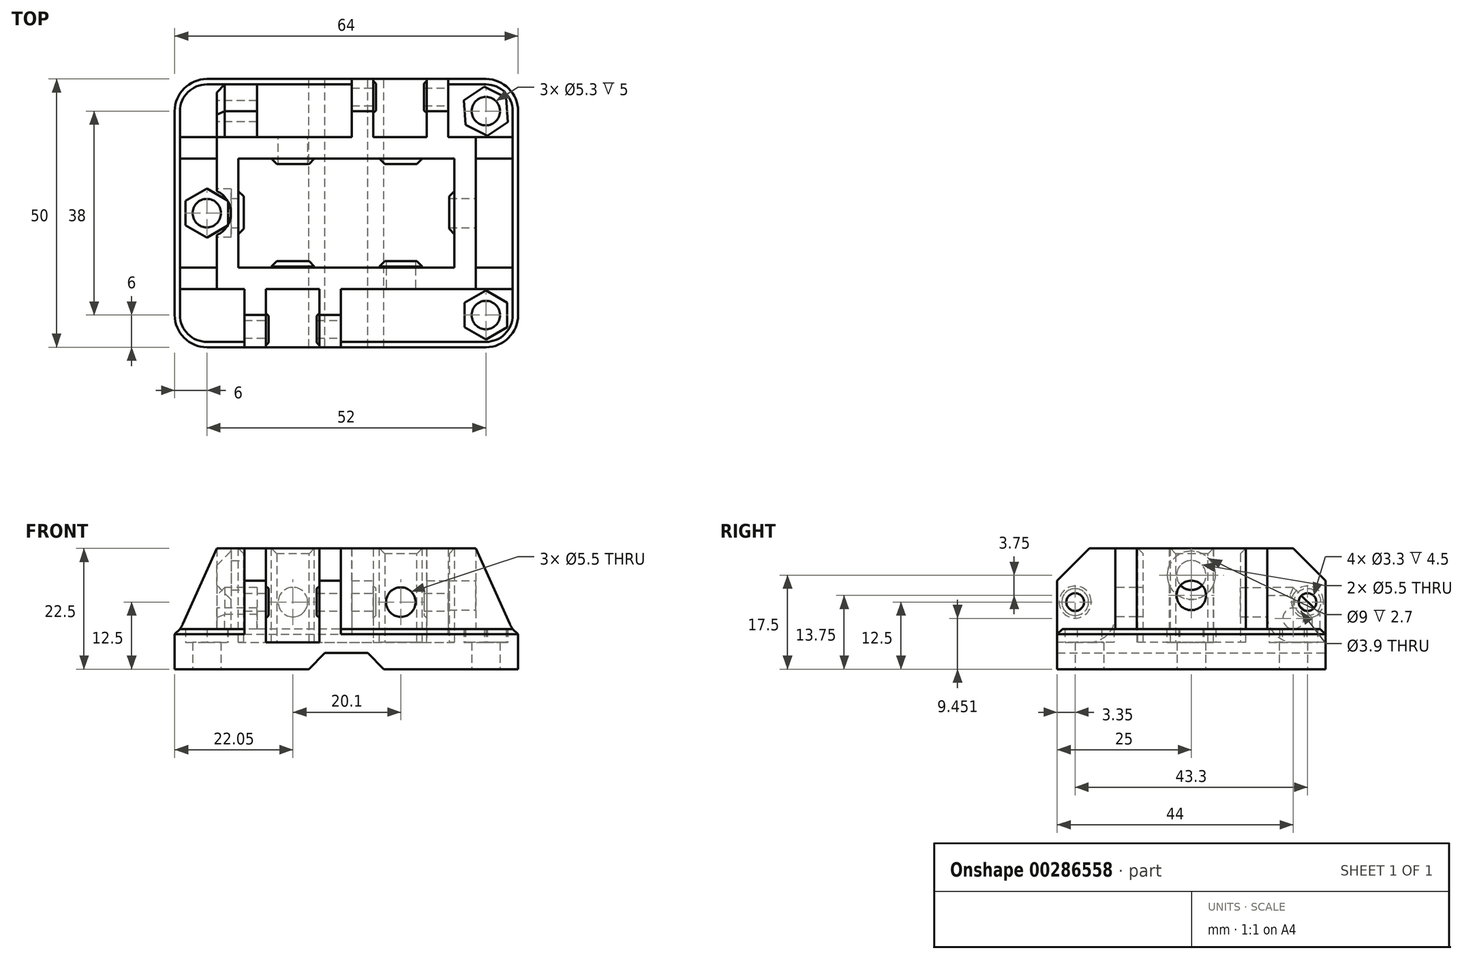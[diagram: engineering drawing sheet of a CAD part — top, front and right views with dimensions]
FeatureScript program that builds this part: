
annotation { "Feature Type Name" : "Feature", "Feature Type Description" : "" }
export const myFeature = defineFeature(function(context is Context, id is Id, definition is map)
    precondition{}
    {
        {
            var Q0;
            Q0=qCreatedBy(makeId("Top.planeOp"),FACE);
            var sketch = newSketch(context, id + "F0", { "sketchPlane" : qUnion([Q0])});
            skLineSegment(sketch, "E0.bottom", {"start": v(0, 0) * mm, "end": v(64, 0) * mm});
            skLineSegment(sketch, "E0.top", {"start": v(0, 50) * mm, "end": v(64, 50) * mm});
            skLineSegment(sketch, "E0.left", {"start": v(0, 0) * mm, "end": v(0, 50) * mm});
            skLineSegment(sketch, "E0.right", {"start": v(64, 0) * mm, "end": v(64, 50) * mm});
            skCircle(sketch, "E1", {"center": v(58, 44) * mm, "radius": 2.65 * mm});
            skPoint(sketch, "E2.centerSnap0", {"position": v(32, 0) * mm});
            skCircle(sketch, "E3", {"center": v(58, 6) * mm, "radius": 2.65 * mm});
            skCircle(sketch, "E4", {"center": v(6, 25) * mm, "radius": 2.65 * mm});
            skPoint(sketch, "E4.centerSnap0", {"position": v(0, 25) * mm});
            skSolve(sketch);
        }
        {
            var Q0;
            Q0=qSketchRegion(id+"F0",true);
            extrude(context, id + "F1", {"entities" : qUnion([Q0]), "depth" : 5 * mm});
        }
        {
            var Q0;
            Q0=makeQuery(id+"F1.opExtrude","CAP_FACE",FACE,{"disambiguationData":[OSD([sQuery(id+"F0.wireOp",EDGE,"E0.bottom"),sQuery(id+"F0.wireOp",EDGE,"E0.top"),sQuery(id+"F0.wireOp",EDGE,"E0.left"),sQuery(id+"F0.wireOp",EDGE,"E0.right"),sQuery(id+"F0.wireOp",EDGE,"SUFVuphh-Qgx9-THfo-SX6n-8QSMb4j17lpz"),sQuery(id+"F0.wireOp",EDGE,"E1"),sQuery(id+"F0.wireOp",EDGE,"E2")])],"isStart":false});
            var sketch = newSketch(context, id + "F2", { "sketchPlane" : qUnion([Q0])});
            skLineSegment(sketch, "E5.bottom", {"start": v(7.85, 39.15) * mm, "end": v(56.15, 39.15) * mm});
            skLineSegment(sketch, "E5.top", {"start": v(7.85, 10.85) * mm, "end": v(56.15, 10.85) * mm});
            skLineSegment(sketch, "E5.left", {"start": v(7.85, 39.15) * mm, "end": v(7.85, 29.1) * mm});
            skLineSegment(sketch, "E5.right", {"start": v(56.15, 39.15) * mm, "end": v(56.15, 10.85) * mm});
            skLineSegment(sketch, "E6.0.0", {"start": v(64, 50) * mm, "end": v(0, 50) * mm, "construction": true});
            skLineSegment(sketch, "E6.0.1", {"start": v(0, 50) * mm, "end": v(0, 0) * mm, "construction": true});
            skLineSegment(sketch, "E6.0.2", {"start": v(0, 0) * mm, "end": v(64, 0) * mm, "construction": true});
            skLineSegment(sketch, "E6.0.3", {"start": v(64, 0) * mm, "end": v(64, 50) * mm, "construction": true});
            skArc(sketch, "E7", {"start": v(7.85, 20.9) * mm, "mid": v(10.5, 25) * mm, "end": v(7.85, 29.1) * mm});
            skLineSegment(sketch, "E8.trimOffspring", {"start": v(7.85, 20.9) * mm, "end": v(7.85, 10.85) * mm});
            skLineSegment(sketch, "E9.bottom", {"start": v(11.85, 35.15) * mm, "end": v(52.15, 35.15) * mm});
            skLineSegment(sketch, "E9.top", {"start": v(11.85, 14.85) * mm, "end": v(52.15, 14.85) * mm});
            skLineSegment(sketch, "E9.left", {"start": v(11.85, 35.15) * mm, "end": v(11.85, 14.85) * mm});
            skLineSegment(sketch, "E9.right", {"start": v(52.15, 35.15) * mm, "end": v(52.15, 14.85) * mm});
            skSolve(sketch);
        }
        {
            var Q0;
            Q0=qSketchRegion(id+"F2",true);
            extrude(context, id + "F3", {"entities" : qUnion([Q0]), "operationType" : NewBodyOperationType.ADD, "depth" : 17.5 * mm});
        }
        {
            var Q0;
            Q0=makeQuery(id+"F3.opExtrude","CAP_FACE",FACE,{"disambiguationData":[OSD([sQuery(id+"F2.wireOp",EDGE,"E5.bottom"),sQuery(id+"F2.wireOp",EDGE,"E5.top"),sQuery(id+"F2.wireOp",EDGE,"E5.left"),sQuery(id+"F2.wireOp",EDGE,"E5.right"),sQuery(id+"F2.wireOp",EDGE,"E7"),sQuery(id+"F2.wireOp",EDGE,"E8.trimOffspring"),sQuery(id+"F2.wireOp",EDGE,"E9.bottom"),sQuery(id+"F2.wireOp",EDGE,"E9.top"),sQuery(id+"F2.wireOp",EDGE,"E9.left"),sQuery(id+"F2.wireOp",EDGE,"E9.right")])],"isStart":false});
            var sketch = newSketch(context, id + "F4", { "sketchPlane" : qUnion([Q0])});
            skLineSegment(sketch, "E10.bottom", {"start": v(11.85, 29.1) * mm, "end": v(12.85, 29.1) * mm});
            skLineSegment(sketch, "E10.top", {"start": v(11.85, 21.1) * mm, "end": v(12.85, 21.1) * mm});
            skLineSegment(sketch, "E10.left", {"start": v(11.85, 29.1) * mm, "end": v(11.85, 21.1) * mm});
            skLineSegment(sketch, "E10.right", {"start": v(12.85, 29.1) * mm, "end": v(12.85, 21.1) * mm});
            skLineSegment(sketch, "E11", {"start": v(32, 35.15) * mm, "end": v(32, 14.85) * mm, "construction": true});
            skLineSegment(sketch, "E12.MirrorCS", {"start": v(52.15, 29.1) * mm, "end": v(51.15, 29.1) * mm});
            skLineSegment(sketch, "E13.MirrorCS", {"start": v(52.15, 21.1) * mm, "end": v(51.15, 21.1) * mm});
            skLineSegment(sketch, "E14.MirrorCS", {"start": v(51.15, 29.1) * mm, "end": v(51.15, 21.1) * mm});
            skLineSegment(sketch, "E15.MirrorCS", {"start": v(52.15, 29.1) * mm, "end": v(52.15, 21.1) * mm});
            skLineSegment(sketch, "E16.bottom", {"start": v(38.15, 35.15) * mm, "end": v(46.15, 35.15) * mm});
            skLineSegment(sketch, "E16.top", {"start": v(38.15, 34.15) * mm, "end": v(46.15, 34.15) * mm});
            skLineSegment(sketch, "E16.left", {"start": v(38.15, 35.15) * mm, "end": v(38.15, 34.15) * mm});
            skLineSegment(sketch, "E16.right", {"start": v(46.15, 35.15) * mm, "end": v(46.15, 34.15) * mm});
            skLineSegment(sketch, "E17.bottom", {"start": v(18.05, 35.15) * mm, "end": v(26.05, 35.15) * mm});
            skLineSegment(sketch, "E17.top", {"start": v(18.05, 34.15) * mm, "end": v(26.05, 34.15) * mm});
            skLineSegment(sketch, "E17.left", {"start": v(18.05, 35.15) * mm, "end": v(18.05, 34.15) * mm});
            skLineSegment(sketch, "E17.right", {"start": v(26.05, 35.15) * mm, "end": v(26.05, 34.15) * mm});
            skLineSegment(sketch, "E18", {"start": v(52.15, 25.1) * mm, "end": v(11.85, 25.1) * mm, "construction": true});
            skLineSegment(sketch, "E19.MirrorCS", {"start": v(38.15, 15.05) * mm, "end": v(38.15, 16.05) * mm});
            skLineSegment(sketch, "E20.MirrorCS", {"start": v(18.05, 15.05) * mm, "end": v(18.05, 16.05) * mm});
            skLineSegment(sketch, "E21.MirrorCS", {"start": v(26.05, 15.05) * mm, "end": v(26.05, 16.05) * mm});
            skLineSegment(sketch, "E22.MirrorCS", {"start": v(46.15, 15.05) * mm, "end": v(46.15, 16.05) * mm});
            skLineSegment(sketch, "E23.MirrorCS", {"start": v(38.15, 15.05) * mm, "end": v(46.15, 15.05) * mm});
            skLineSegment(sketch, "E24.MirrorCS", {"start": v(18.05, 16.05) * mm, "end": v(26.05, 16.05) * mm});
            skLineSegment(sketch, "E25.MirrorCS", {"start": v(18.05, 15.05) * mm, "end": v(26.05, 15.05) * mm});
            skLineSegment(sketch, "E26.MirrorCS", {"start": v(38.15, 16.05) * mm, "end": v(46.15, 16.05) * mm});
            skSolve(sketch);
        }
        {
            var Q0;
            Q0=qSketchRegion(id+"F4",true);
            var Q1;
            Q1=makeQuery(id+"F3.boolean.opBoolean","SPLIT",FACE,{"disambiguationData":[TD([makeQuery(id+"F3.opExtrude","SWEPT_FACE",FACE,{"disambiguationData":[OSD([sQuery(id+"F2.wireOp",EDGE,"E9.bottom")])]})])],"derivedFrom":makeQuery(id+"F1.opExtrude","CAP_FACE",FACE,{"disambiguationData":[OSD([sQuery(id+"F0.wireOp",EDGE,"E0.bottom"),sQuery(id+"F0.wireOp",EDGE,"E0.top"),sQuery(id+"F0.wireOp",EDGE,"E0.left"),sQuery(id+"F0.wireOp",EDGE,"E0.right"),sQuery(id+"F0.wireOp",EDGE,"E1"),sQuery(id+"F0.wireOp",EDGE,"E3"),sQuery(id+"F0.wireOp",EDGE,"E4")])],"isStart":false})});
            extrude(context, id + "F5", {"entities" : qUnion([Q0]), "operationType" : NewBodyOperationType.ADD, "endBound" : BoundingType.UP_TO_SURFACE, "oppositeDirection" : true, "endBoundEntityFace" : qUnion([Q1]), "depth" : 25 * mm});
        }
        {
            var Q0;
            Q0=makeQuery(id+"F5.opExtrude","SWEPT_EDGE",EDGE,{"disambiguationData":[OSD([sQuery(id+"F4.wireOp",EDGE,"E10.bottom"),sQuery(id+"F4.wireOp",EDGE,"E10.right")])]});
            var Q1;
            Q1=makeQuery(id+"F5.opExtrude","SWEPT_EDGE",EDGE,{"disambiguationData":[OSD([sQuery(id+"F4.wireOp",EDGE,"E10.top"),sQuery(id+"F4.wireOp",EDGE,"E10.right")])]});
            var Q2;
            Q2=makeQuery(id+"F5.opExtrude","CAP_EDGE",EDGE,{"disambiguationData":[OSD([sQuery(id+"F4.wireOp",EDGE,"E10.right")])],"isStart":true});
            var Q3;
            Q3=makeQuery(id+"F5.opExtrude","SWEPT_EDGE",EDGE,{"disambiguationData":[OSD([sQuery(id+"F4.wireOp",EDGE,"E12.MirrorCS"),sQuery(id+"F4.wireOp",EDGE,"E14.MirrorCS")])]});
            var Q4;
            Q4=makeQuery(id+"F5.opExtrude","SWEPT_EDGE",EDGE,{"disambiguationData":[OSD([sQuery(id+"F4.wireOp",EDGE,"E13.MirrorCS"),sQuery(id+"F4.wireOp",EDGE,"E14.MirrorCS")])]});
            var Q5;
            Q5=makeQuery(id+"F5.opExtrude","CAP_EDGE",EDGE,{"disambiguationData":[OSD([sQuery(id+"F4.wireOp",EDGE,"E14.MirrorCS")])],"isStart":true});
            var Q6;
            Q6=makeQuery(id+"F5.opExtrude","SWEPT_EDGE",EDGE,{"disambiguationData":[OSD([sQuery(id+"F4.wireOp",EDGE,"E17.top"),sQuery(id+"F4.wireOp",EDGE,"E17.left")])]});
            var Q7;
            Q7=makeQuery(id+"F5.opExtrude","CAP_EDGE",EDGE,{"disambiguationData":[OSD([sQuery(id+"F4.wireOp",EDGE,"E17.top")])],"isStart":true});
            var Q8;
            Q8=makeQuery(id+"F5.opExtrude","SWEPT_EDGE",EDGE,{"disambiguationData":[OSD([sQuery(id+"F4.wireOp",EDGE,"E17.top"),sQuery(id+"F4.wireOp",EDGE,"E17.right")])]});
            var Q9;
            Q9=makeQuery(id+"F5.opExtrude","SWEPT_EDGE",EDGE,{"disambiguationData":[OSD([sQuery(id+"F4.wireOp",EDGE,"E16.top"),sQuery(id+"F4.wireOp",EDGE,"E16.left")])]});
            var Q10;
            Q10=makeQuery(id+"F5.opExtrude","CAP_EDGE",EDGE,{"disambiguationData":[OSD([sQuery(id+"F4.wireOp",EDGE,"E16.top")])],"isStart":true});
            var Q11;
            Q11=makeQuery(id+"F5.opExtrude","SWEPT_EDGE",EDGE,{"disambiguationData":[OSD([sQuery(id+"F4.wireOp",EDGE,"E16.top"),sQuery(id+"F4.wireOp",EDGE,"E16.right")])]});
            var Q12;
            Q12=makeQuery(id+"F5.opExtrude","CAP_EDGE",EDGE,{"disambiguationData":[OSD([sQuery(id+"F4.wireOp",EDGE,"E26.MirrorCS")])],"isStart":true});
            var Q13;
            Q13=makeQuery(id+"F5.opExtrude","CAP_EDGE",EDGE,{"disambiguationData":[OSD([sQuery(id+"F4.wireOp",EDGE,"E24.MirrorCS")])],"isStart":true});
            var Q14;
            Q14=makeQuery(id+"F5.opExtrude","SWEPT_EDGE",EDGE,{"disambiguationData":[OSD([sQuery(id+"F4.wireOp",EDGE,"E20.MirrorCS"),sQuery(id+"F4.wireOp",EDGE,"E24.MirrorCS")])]});
            var Q15;
            Q15=makeQuery(id+"F5.opExtrude","SWEPT_EDGE",EDGE,{"disambiguationData":[OSD([sQuery(id+"F4.wireOp",EDGE,"E21.MirrorCS"),sQuery(id+"F4.wireOp",EDGE,"E24.MirrorCS")])]});
            var Q16;
            Q16=makeQuery(id+"F5.opExtrude","SWEPT_EDGE",EDGE,{"disambiguationData":[OSD([sQuery(id+"F4.wireOp",EDGE,"E19.MirrorCS"),sQuery(id+"F4.wireOp",EDGE,"E26.MirrorCS")])]});
            var Q17;
            Q17=makeQuery(id+"F5.opExtrude","SWEPT_EDGE",EDGE,{"disambiguationData":[OSD([sQuery(id+"F4.wireOp",EDGE,"E22.MirrorCS"),sQuery(id+"F4.wireOp",EDGE,"E26.MirrorCS")])]});
            chamfer(context, id + "F6", {"entities" : qUnion([Q0, Q1, Q2, Q3, Q4, Q5, Q6, Q7, Q8, Q9, Q10, Q11, Q12, Q13, Q14, Q15, Q16, Q17]), "width" : 1 * mm, "tangentPropagation" : true});
        }
        {
            var Q0;
            Q0=makeQuery(id+"F1.opExtrude","SWEPT_EDGE",EDGE,{"disambiguationData":[OSD([sQuery(id+"F0.wireOp",EDGE,"E0.bottom"),sQuery(id+"F0.wireOp",EDGE,"E0.right")])]});
            var Q1;
            Q1=makeQuery(id+"F1.opExtrude","SWEPT_EDGE",EDGE,{"disambiguationData":[OSD([sQuery(id+"F0.wireOp",EDGE,"E0.top"),sQuery(id+"F0.wireOp",EDGE,"E0.left")])]});
            var Q2;
            Q2=makeQuery(id+"F1.opExtrude","SWEPT_EDGE",EDGE,{"disambiguationData":[OSD([sQuery(id+"F0.wireOp",EDGE,"E0.top"),sQuery(id+"F0.wireOp",EDGE,"E0.right")])]});
            var Q3;
            Q3=makeQuery(id+"F1.opExtrude","SWEPT_EDGE",EDGE,{"disambiguationData":[OSD([sQuery(id+"F0.wireOp",EDGE,"E0.bottom"),sQuery(id+"F0.wireOp",EDGE,"E0.left")])]});
            fillet(context, id + "F7", {"entities" : qUnion([Q0, Q1, Q2, Q3]), "radius" : 6 * mm, "tangentPropagation" : true, "allowEdgeOverflow" : false});
        }
        {
            var Q0;
            {var subQ0=sQuery(id+"F0.wireOp",EDGE,"E0.left");var subQ1=sQuery(id+"F0.wireOp",EDGE,"E4");var subQ2=sQuery(id+"F0.wireOp",EDGE,"E3");var subQ3=sQuery(id+"F0.wireOp",EDGE,"E1");var subQ4=sQuery(id+"F0.wireOp",EDGE,"E0.bottom");var subQ5=sQuery(id+"F0.wireOp",EDGE,"E0.right");var subQ6=sQuery(id+"F0.wireOp",EDGE,"E0.top");Q0=makeQuery(id+"F3.boolean.opBoolean","SPLIT",FACE,{"disambiguationData":[TD([makeQuery(id+"F1.opExtrude","SWEPT_FACE",FACE,{"disambiguationData":[OSD([subQ4])]})])],"derivedFrom":makeQuery(id+"F1.opExtrude","CAP_FACE",FACE,{"disambiguationData":[OSD([subQ4,subQ6,subQ0,subQ5,subQ3,subQ2,subQ1])],"isStart":false})});}
            var sketch = newSketch(context, id + "F8", { "sketchPlane" : qUnion([Q0])});
            skLineSegment(sketch, "E27.bottom", {"start": v(7.85, 39.15) * mm, "end": v(0, 39.15) * mm});
            skLineSegment(sketch, "E27.top", {"start": v(7.85, 35.15) * mm, "end": v(0, 35.15) * mm});
            skLineSegment(sketch, "E27.left", {"start": v(7.85, 39.15) * mm, "end": v(7.85, 35.15) * mm});
            skLineSegment(sketch, "E27.right", {"start": v(0, 39.15) * mm, "end": v(0, 35.15) * mm});
            skLineSegment(sketch, "E28.bottom", {"start": v(7.85, 10.85) * mm, "end": v(0, 10.85) * mm});
            skLineSegment(sketch, "E28.top", {"start": v(7.85, 14.85) * mm, "end": v(0, 14.85) * mm});
            skLineSegment(sketch, "E28.left", {"start": v(7.85, 10.85) * mm, "end": v(7.85, 14.85) * mm});
            skLineSegment(sketch, "E28.right", {"start": v(0, 10.85) * mm, "end": v(0, 14.85) * mm});
            skLineSegment(sketch, "E29.bottom", {"start": v(56.15, 39.15) * mm, "end": v(64, 39.15) * mm});
            skLineSegment(sketch, "E29.top", {"start": v(56.15, 35.15) * mm, "end": v(64, 35.15) * mm});
            skLineSegment(sketch, "E29.left", {"start": v(56.15, 39.15) * mm, "end": v(56.15, 35.15) * mm});
            skLineSegment(sketch, "E29.right", {"start": v(64, 39.15) * mm, "end": v(64, 35.15) * mm});
            skLineSegment(sketch, "E30.bottom", {"start": v(56.15, 10.85) * mm, "end": v(64, 10.85) * mm});
            skLineSegment(sketch, "E30.top", {"start": v(56.15, 14.85) * mm, "end": v(64, 14.85) * mm});
            skLineSegment(sketch, "E30.left", {"start": v(56.15, 10.85) * mm, "end": v(56.15, 14.85) * mm});
            skLineSegment(sketch, "E30.right", {"start": v(64, 10.85) * mm, "end": v(64, 14.85) * mm});
            skLineSegment(sketch, "E31.bottom", {"start": v(7.85, 10.85) * mm, "end": v(12.5, 10.85) * mm});
            skLineSegment(sketch, "E32.bottom", {"start": v(7.85, 39.15) * mm, "end": v(12.5, 39.15) * mm});
            skLineSegment(sketch, "E33.0.0", {"start": v(7.85, 20.9) * mm, "end": v(7.85, 10.85) * mm, "construction": true});
            skLineSegment(sketch, "E33.0.1", {"start": v(12.5, 10.85) * mm, "end": v(48.25, 10.85) * mm, "construction": true});
            skLineSegment(sketch, "E33.0.2", {"start": v(56.15, 10.85) * mm, "end": v(56.15, 39.15) * mm, "construction": true});
            skLineSegment(sketch, "E33.0.3", {"start": v(56.15, 39.15) * mm, "end": v(12.5, 39.15) * mm, "construction": true});
            skLineSegment(sketch, "E33.0.4", {"start": v(7.85, 39.15) * mm, "end": v(7.85, 29.1) * mm, "construction": true});
            skArc(sketch, "E33.0.5", {"start": v(7.85, 29.1) * mm, "mid": v(10.5, 25) * mm, "end": v(7.85, 20.9) * mm, "construction": true});
            skLineSegment(sketch, "E34.0", {"start": v(52.15, 35.15) * mm, "end": v(52.15, 29.1) * mm, "construction": true});
            skLineSegment(sketch, "E35.0", {"start": v(52.15, 21.1) * mm, "end": v(52.15, 14.85) * mm, "construction": true});
            skLineSegment(sketch, "E36.bottom", {"start": v(51, 39.15) * mm, "end": v(47, 39.15) * mm});
            skLineSegment(sketch, "E36.top", {"start": v(51, 50) * mm, "end": v(47, 50) * mm});
            skLineSegment(sketch, "E36.left", {"start": v(51, 39.15) * mm, "end": v(51, 50) * mm});
            skLineSegment(sketch, "E36.right", {"start": v(47, 39.15) * mm, "end": v(47, 50) * mm});
            skLineSegment(sketch, "E37.bottom", {"start": v(37, 50) * mm, "end": v(33, 50) * mm});
            skLineSegment(sketch, "E37.top", {"start": v(37, 39.15) * mm, "end": v(33, 39.15) * mm});
            skLineSegment(sketch, "E37.left", {"start": v(37, 50) * mm, "end": v(37, 39.15) * mm});
            skLineSegment(sketch, "E37.right", {"start": v(33, 50) * mm, "end": v(33, 39.15) * mm});
            skLineSegment(sketch, "E38.bottom", {"start": v(27, 10.85) * mm, "end": v(31, 10.85) * mm});
            skLineSegment(sketch, "E38.top", {"start": v(27, 0) * mm, "end": v(31, 0) * mm});
            skLineSegment(sketch, "E38.left", {"start": v(27, 10.85) * mm, "end": v(27, 0) * mm});
            skLineSegment(sketch, "E38.right", {"start": v(31, 10.85) * mm, "end": v(31, 0) * mm});
            skLineSegment(sketch, "E39.bottom", {"start": v(17, 10.85) * mm, "end": v(13, 10.85) * mm});
            skLineSegment(sketch, "E39.top", {"start": v(17, 0) * mm, "end": v(13, 0) * mm});
            skLineSegment(sketch, "E39.left", {"start": v(17, 10.85) * mm, "end": v(17, 0) * mm});
            skLineSegment(sketch, "E39.right", {"start": v(13, 10.85) * mm, "end": v(13, 0) * mm});
            skLineSegment(sketch, "E40.trimOffspring", {"start": v(52.15, 10.85) * mm, "end": v(56.15, 10.85) * mm, "construction": true});
            skSolve(sketch);
        }
        {
            var Q0;
            Q0=qSketchRegion(id+"F8",true);
            var Q1;
            Q1=makeQuery(id+"F5.boolean.opBoolean","MERGE",FACE,{"derivedFrom":[makeQuery(id+"F3.opExtrude","CAP_FACE",FACE,{"disambiguationData":[OSD([sQuery(id+"F2.wireOp",EDGE,"E5.bottom"),sQuery(id+"F2.wireOp",EDGE,"E5.top"),sQuery(id+"F2.wireOp",EDGE,"E5.left"),sQuery(id+"F2.wireOp",EDGE,"E5.right"),sQuery(id+"F2.wireOp",EDGE,"E7"),sQuery(id+"F2.wireOp",EDGE,"E8.trimOffspring"),sQuery(id+"F2.wireOp",EDGE,"E9.bottom"),sQuery(id+"F2.wireOp",EDGE,"E9.top"),sQuery(id+"F2.wireOp",EDGE,"E9.left"),sQuery(id+"F2.wireOp",EDGE,"E9.right")])],"isStart":false}),makeQuery(id+"F5.opExtrude","CAP_FACE",FACE,{"disambiguationData":[OSD([sQuery(id+"F4.wireOp",EDGE,"E10.bottom"),sQuery(id+"F4.wireOp",EDGE,"E10.top"),sQuery(id+"F4.wireOp",EDGE,"E10.left"),sQuery(id+"F4.wireOp",EDGE,"E10.right")])],"isStart":true}),makeQuery(id+"F5.opExtrude","CAP_FACE",FACE,{"disambiguationData":[OSD([sQuery(id+"F4.wireOp",EDGE,"E12.MirrorCS"),sQuery(id+"F4.wireOp",EDGE,"E13.MirrorCS"),sQuery(id+"F4.wireOp",EDGE,"E14.MirrorCS"),sQuery(id+"F4.wireOp",EDGE,"E15.MirrorCS")])],"isStart":true}),makeQuery(id+"F5.opExtrude","CAP_FACE",FACE,{"disambiguationData":[OSD([sQuery(id+"F4.wireOp",EDGE,"E16.bottom"),sQuery(id+"F4.wireOp",EDGE,"E16.top"),sQuery(id+"F4.wireOp",EDGE,"E16.left"),sQuery(id+"F4.wireOp",EDGE,"E16.right")])],"isStart":true}),makeQuery(id+"F5.opExtrude","CAP_FACE",FACE,{"disambiguationData":[OSD([sQuery(id+"F4.wireOp",EDGE,"E17.bottom"),sQuery(id+"F4.wireOp",EDGE,"E17.top"),sQuery(id+"F4.wireOp",EDGE,"E17.left"),sQuery(id+"F4.wireOp",EDGE,"E17.right")])],"isStart":true})]});
            extrude(context, id + "F9", {"entities" : qUnion([Q0]), "operationType" : NewBodyOperationType.ADD, "endBound" : BoundingType.UP_TO_SURFACE, "endBoundEntityFace" : qUnion([Q1]), "depth" : 25 * mm});
        }
        {
            var Q0;
            {var subQ0=makeQuery(id+"F9.opExtrude","SWEPT_FACE",FACE,{"disambiguationData":[OSD([sQuery(id+"F8.wireOp",EDGE,"E30.bottom")])]});var subQ1=makeQuery(id+"F9.opExtrude","SWEPT_FACE",FACE,{"disambiguationData":[OSD([sQuery(id+"F8.wireOp",EDGE,"E28.bottom")])]});var subQ2=makeQuery(id+"F3.opExtrude","SWEPT_FACE",FACE,{"disambiguationData":[OSD([sQuery(id+"F2.wireOp",EDGE,"E5.top")])]});Q0=qUnion([makeQuery(id+"F9.boolean.opBoolean","MERGE",FACE,{"disambiguationData":[OD(2.0)],"derivedFrom":[subQ2,subQ1,subQ0]}),makeQuery(id+"F9.boolean.opBoolean","MERGE",FACE,{"disambiguationData":[OD(0.0)],"derivedFrom":[subQ2,subQ1,subQ0]}),makeQuery(id+"F9.boolean.opBoolean","MERGE",FACE,{"disambiguationData":[OD(1.0)],"derivedFrom":[subQ2,subQ1,subQ0]})]);}
            var sketch = newSketch(context, id + "F10", { "sketchPlane" : qUnion([Q0])});
            skLineSegment(sketch, "E41", {"start": v(0, 5) * mm, "end": v(0, 22.5) * mm});
            skLineSegment(sketch, "E42.0.0", {"start": v(64, 22.5) * mm, "end": v(56.15, 22.5) * mm, "construction": true});
            skLineSegment(sketch, "E42.0.1", {"start": v(56.15, 22.5) * mm, "end": v(56.15, 5) * mm, "construction": true});
            skLineSegment(sketch, "E42.0.2", {"start": v(56.15, 5) * mm, "end": v(64, 5) * mm, "construction": true});
            skLineSegment(sketch, "E42.0.3", {"start": v(64, 5) * mm, "end": v(64, 22.5) * mm});
            skLineSegment(sketch, "E43", {"start": v(56.15, 22.5) * mm, "end": v(64, 22.5) * mm});
            skLineSegment(sketch, "E44", {"start": v(64, 5) * mm, "end": v(56.15, 22.5) * mm});
            skLineSegment(sketch, "E45.0.1", {"start": v(7.85, 22.5) * mm, "end": v(7.85, 5) * mm, "construction": true});
            skLineSegment(sketch, "E45.0.3", {"start": v(7.85, 5) * mm, "end": v(7.85, 22.5) * mm, "construction": true});
            skLineSegment(sketch, "E46", {"start": v(0, 22.5) * mm, "end": v(7.85, 22.5) * mm});
            skLineSegment(sketch, "E47", {"start": v(0, 5) * mm, "end": v(7.85, 22.5) * mm});
            skSolve(sketch);
        }
        {
            var Q0;
            Q0=qSketchRegion(id+"F10",true);
            var Q1;
            {var subQ0=makeQuery(id+"F9.opExtrude","SWEPT_FACE",FACE,{"disambiguationData":[OSD([sQuery(id+"F8.wireOp",EDGE,"E29.bottom")])]});var subQ1=makeQuery(id+"F9.opExtrude","SWEPT_FACE",FACE,{"disambiguationData":[OSD([sQuery(id+"F8.wireOp",EDGE,"E27.bottom")])]});var subQ2=makeQuery(id+"F3.opExtrude","SWEPT_FACE",FACE,{"disambiguationData":[OSD([sQuery(id+"F2.wireOp",EDGE,"E5.bottom")])]});Q1=qUnion([makeQuery(id+"F9.boolean.opBoolean","MERGE",FACE,{"disambiguationData":[OD(1.0)],"derivedFrom":[subQ2,subQ1,subQ0]}),makeQuery(id+"F9.boolean.opBoolean","MERGE",FACE,{"disambiguationData":[OD(2.0)],"derivedFrom":[subQ2,subQ1,subQ0]}),makeQuery(id+"F9.boolean.opBoolean","MERGE",FACE,{"disambiguationData":[OD(0.0)],"derivedFrom":[subQ2,subQ1,subQ0]})]);}
            extrude(context, id + "F11", {"entities" : qUnion([Q0]), "operationType" : NewBodyOperationType.REMOVE, "endBound" : BoundingType.UP_TO_SURFACE, "oppositeDirection" : true, "endBoundEntityFace" : qUnion([Q1]), "depth" : 25 * mm});
        }
        {
            var Q0;
            Q0=makeQuery(id+"F3.opExtrude","SWEPT_FACE",FACE,{"disambiguationData":[OSD([sQuery(id+"F2.wireOp",EDGE,"E5.right")])]});
            var sketch = newSketch(context, id + "F12", { "sketchPlane" : qUnion([Q0])});
            skCircle(sketch, "E48", {"center": v(25, 13.75) * mm, "radius": 2.75 * mm});
            skPoint(sketch, "E48.centerSnap0", {"position": v(35.15, 13.75) * mm});
            skPoint(sketch, "E48.centerSnap1", {"position": v(25, 22.5) * mm});
            skSolve(sketch);
        }
        {
            var Q0;
            Q0=qSketchRegion(id+"F12",true);
            var Q1;
            Q1=makeQuery(id+"F5.opExtrude","SWEPT_FACE",FACE,{"disambiguationData":[OSD([sQuery(id+"F4.wireOp",EDGE,"E14.MirrorCS")])]});
            extrude(context, id + "F13", {"entities" : qUnion([Q0]), "operationType" : NewBodyOperationType.REMOVE, "endBound" : BoundingType.UP_TO_SURFACE, "oppositeDirection" : true, "endBoundEntityFace" : qUnion([Q1]), "depth" : 25 * mm});
        }
        {
            var Q0;
            Q0=makeQuery(id+"F9.boolean.opBoolean","MERGE",FACE,{"disambiguationData":[OD(1.0)],"derivedFrom":[makeQuery(id+"F3.opExtrude","SWEPT_FACE",FACE,{"disambiguationData":[OSD([sQuery(id+"F2.wireOp",EDGE,"E5.bottom")])]}),makeQuery(id+"F9.opExtrude","SWEPT_FACE",FACE,{"disambiguationData":[OSD([sQuery(id+"F8.wireOp",EDGE,"E27.bottom")])]}),makeQuery(id+"F9.opExtrude","SWEPT_FACE",FACE,{"disambiguationData":[OSD([sQuery(id+"F8.wireOp",EDGE,"E29.bottom")])]})]});
            var sketch = newSketch(context, id + "F14", { "sketchPlane" : qUnion([Q0])});
            skCircle(sketch, "E49", {"center": v(-42.15, 12.5) * mm, "radius": 2.75 * mm, "construction": true});
            skPoint(sketch, "E49.centerSnap0", {"position": v(-47.15, 12.5) * mm});
            skLineSegment(sketch, "E50.0.0", {"start": v(-39.15, 5) * mm, "end": v(-45.15, 5) * mm, "construction": true});
            skLineSegment(sketch, "E50.0.1", {"start": v(-45.15, 5) * mm, "end": v(-45.15, 21.5) * mm, "construction": true});
            skLineSegment(sketch, "E50.0.2", {"start": v(-45.15, 21.5) * mm, "end": v(-39.15, 21.5) * mm, "construction": true});
            skLineSegment(sketch, "E50.0.3", {"start": v(-39.15, 21.5) * mm, "end": v(-39.15, 5) * mm, "construction": true});
            skLineSegment(sketch, "E51.0.0", {"start": v(-19.05, 5) * mm, "end": v(-25.05, 5) * mm, "construction": true});
            skLineSegment(sketch, "E51.0.1", {"start": v(-25.05, 5) * mm, "end": v(-25.05, 21.5) * mm, "construction": true});
            skLineSegment(sketch, "E51.0.2", {"start": v(-25.05, 21.5) * mm, "end": v(-19.05, 21.5) * mm, "construction": true});
            skLineSegment(sketch, "E51.0.3", {"start": v(-19.05, 21.5) * mm, "end": v(-19.05, 5) * mm, "construction": true});
            skCircle(sketch, "E52", {"center": v(-22.05, 12.5) * mm, "radius": 2.75 * mm});
            skPoint(sketch, "E52.centerSnap0", {"position": v(-22.05, 21.5) * mm});
            skSolve(sketch);
        }
        {
            var Q0;
            Q0=qSketchRegion(id+"F14",true);
            var Q1;
            Q1=makeQuery(id+"F5.opExtrude","SWEPT_FACE",FACE,{"disambiguationData":[OSD([sQuery(id+"F4.wireOp",EDGE,"E17.top")])]});
            extrude(context, id + "F15", {"entities" : qUnion([Q0]), "operationType" : NewBodyOperationType.REMOVE, "endBound" : BoundingType.UP_TO_SURFACE, "oppositeDirection" : true, "endBoundEntityFace" : qUnion([Q1]), "depth" : 25 * mm});
        }
        {
            var Q0;
            Q0=makeQuery(id+"F9.opExtrude","SWEPT_FACE",FACE,{"disambiguationData":[OSD([sQuery(id+"F8.wireOp",EDGE,"E36.left")])]});
            var sketch = newSketch(context, id + "F16", { "sketchPlane" : qUnion([Q0])});
            skCircle(sketch, "E53", {"center": v(46.65, 12.5) * mm, "radius": 1.65 * mm});
            skLineSegment(sketch, "E54.0.0", {"start": v(35.15, 22.5) * mm, "end": v(14.85, 22.5) * mm, "construction": true});
            skLineSegment(sketch, "E54.0.1", {"start": v(14.85, 22.5) * mm, "end": v(14.85, 5) * mm, "construction": true});
            skLineSegment(sketch, "E54.0.2", {"start": v(14.85, 5) * mm, "end": v(35.15, 5) * mm, "construction": true});
            skLineSegment(sketch, "E54.0.3", {"start": v(35.15, 5) * mm, "end": v(35.15, 22.5) * mm, "construction": true});
            skLineSegment(sketch, "E55", {"start": v(25, 22.5) * mm, "end": v(25, 5) * mm, "construction": true});
            skCircle(sketch, "E56.MirrorC", {"center": v(3.35, 12.5) * mm, "radius": 1.65 * mm});
            skSolve(sketch);
        }
        {
            var Q0;
            Q0=qSketchRegion(id+"F16",true);
            extrude(context, id + "F17", {"entities" : qUnion([Q0]), "operationType" : NewBodyOperationType.REMOVE, "endBound" : BoundingType.THROUGH_ALL, "oppositeDirection" : true, "depth" : 25 * mm});
        }
        {
            var Q0;
            Q0=makeQuery(id+"F9.opExtrude","CAP_EDGE",EDGE,{"disambiguationData":[OSD([sQuery(id+"F8.wireOp",EDGE,"E36.top")])],"isStart":false});
            var Q1;
            Q1=makeQuery(id+"F9.opExtrude","CAP_EDGE",EDGE,{"disambiguationData":[OSD([sQuery(id+"F8.wireOp",EDGE,"E37.bottom")])],"isStart":false});
            var Q2;
            Q2=makeQuery(id+"F9.opExtrude","CAP_EDGE",EDGE,{"disambiguationData":[OSD([sQuery(id+"F8.wireOp",EDGE,"E39.top")])],"isStart":false});
            var Q3;
            Q3=makeQuery(id+"F9.opExtrude","CAP_EDGE",EDGE,{"disambiguationData":[OSD([sQuery(id+"F8.wireOp",EDGE,"E38.top")])],"isStart":false});
            chamfer(context, id + "F18", {"entities" : qUnion([Q0, Q1, Q2, Q3]), "width" : 6 * mm, "tangentPropagation" : true});
        }
        {
            var Q0;
            Q0=makeQuery(id+"F3.opExtrude","SWEPT_FACE",FACE,{"disambiguationData":[OSD([sQuery(id+"F2.wireOp",EDGE,"E5.left")])]});
            var sketch = newSketch(context, id + "F19", { "sketchPlane" : qUnion([Q0])});
            skCircle(sketch, "E57", {"center": v(-25, 17.5) * mm, "radius": 4.5 * mm});
            skSolve(sketch);
        }
        {
            var Q0;
            Q0=qSketchRegion(id+"F19",true);
            extrude(context, id + "F20", {"entities" : qUnion([Q0]), "operationType" : NewBodyOperationType.REMOVE, "oppositeDirection" : true, "depth" : 2.7 * mm});
        }
        {
            var Q0;
            Q0=makeQuery(id+"F9.boolean.opBoolean","MERGE",FACE,{"disambiguationData":[OD(1.0)],"derivedFrom":[makeQuery(id+"F3.opExtrude","SWEPT_FACE",FACE,{"disambiguationData":[OSD([sQuery(id+"F2.wireOp",EDGE,"E5.top")])]}),makeQuery(id+"F9.opExtrude","SWEPT_FACE",FACE,{"disambiguationData":[OSD([sQuery(id+"F8.wireOp",EDGE,"E28.bottom")])]}),makeQuery(id+"F9.opExtrude","SWEPT_FACE",FACE,{"disambiguationData":[OSD([sQuery(id+"F8.wireOp",EDGE,"E30.bottom")])]})]});
            var sketch = newSketch(context, id + "F21", { "sketchPlane" : qUnion([Q0])});
            skLineSegment(sketch, "E58.0.3", {"start": v(31, 22.5) * mm, "end": v(56.15, 22.5) * mm, "construction": true});
            skLineSegment(sketch, "E59.0.0", {"start": v(39.15, 21.5) * mm, "end": v(45.15, 21.5) * mm, "construction": true});
            skLineSegment(sketch, "E59.0.1", {"start": v(45.15, 21.5) * mm, "end": v(45.15, 5) * mm, "construction": true});
            skLineSegment(sketch, "E59.0.2", {"start": v(45.15, 5) * mm, "end": v(39.15, 5) * mm, "construction": true});
            skLineSegment(sketch, "E59.0.3", {"start": v(39.15, 5) * mm, "end": v(39.15, 21.5) * mm, "construction": true});
            skCircle(sketch, "E60", {"center": v(42.15, 12.5) * mm, "radius": 2.75 * mm});
            skPoint(sketch, "E60.centerSnap0", {"position": v(42.15, 21.5) * mm});
            skSolve(sketch);
        }
        {
            var Q0;
            Q0=qSketchRegion(id+"F21",true);
            var Q1;
            Q1=makeQuery(id+"F5.opExtrude","SWEPT_FACE",FACE,{"disambiguationData":[OSD([sQuery(id+"F4.wireOp",EDGE,"E26.MirrorCS")])]});
            extrude(context, id + "F22", {"entities" : qUnion([Q0]), "operationType" : NewBodyOperationType.REMOVE, "endBound" : BoundingType.UP_TO_SURFACE, "oppositeDirection" : true, "endBoundEntityFace" : qUnion([Q1]), "depth" : 25 * mm});
        }
        {
            var Q0;
            Q0=makeQuery(id+"F9.opExtrude","SWEPT_FACE",FACE,{"disambiguationData":[OSD([sQuery(id+"F8.wireOp",EDGE,"E36.right")])]});
            var sketch = newSketch(context, id + "F23", { "sketchPlane" : qUnion([Q0])});
            skCircle(sketch, "E61.0", {"center": v(-46.65, 12.5) * mm, "radius": 1.65 * mm});
            skCircle(sketch, "E62", {"center": v(-46.65, 12.5) * mm, "radius": 3 * mm});
            skSolve(sketch);
        }
        {
            var Q0;
            Q0=qSketchRegion(id+"F23",true);
            extrude(context, id + "F24", {"entities" : qUnion([Q0]), "operationType" : NewBodyOperationType.ADD, "depth" : .5 * mm});
        }
        {
            var Q0;
            Q0=makeQuery(id+"F9.opExtrude","SWEPT_FACE",FACE,{"disambiguationData":[OSD([sQuery(id+"F8.wireOp",EDGE,"E37.left")])]});
            var sketch = newSketch(context, id + "F25", { "sketchPlane" : qUnion([Q0])});
            skCircle(sketch, "E63.0", {"center": v(46.65, 12.5) * mm, "radius": 1.65 * mm});
            skCircle(sketch, "E64", {"center": v(46.65, 12.5) * mm, "radius": 3 * mm});
            skSolve(sketch);
        }
        {
            var Q0;
            Q0=qSketchRegion(id+"F25",true);
            extrude(context, id + "F26", {"entities" : qUnion([Q0]), "operationType" : NewBodyOperationType.ADD, "depth" : .5 * mm});
        }
        {
            var Q0;
            Q0=makeQuery(id+"F9.opExtrude","SWEPT_FACE",FACE,{"disambiguationData":[OSD([sQuery(id+"F8.wireOp",EDGE,"E38.left")])]});
            var sketch = newSketch(context, id + "F27", { "sketchPlane" : qUnion([Q0])});
            skCircle(sketch, "E65", {"center": v(-3.35, 12.5) * mm, "radius": 3 * mm});
            skCircle(sketch, "E66.0", {"center": v(-3.35, 12.5) * mm, "radius": 1.65 * mm});
            skSolve(sketch);
        }
        {
            var Q0;
            Q0=qSketchRegion(id+"F27",true);
            extrude(context, id + "F28", {"entities" : qUnion([Q0]), "operationType" : NewBodyOperationType.ADD, "depth" : .5 * mm});
        }
        {
            var Q0;
            Q0=makeQuery(id+"F9.opExtrude","SWEPT_FACE",FACE,{"disambiguationData":[OSD([sQuery(id+"F8.wireOp",EDGE,"E39.left")])]});
            var sketch = newSketch(context, id + "F29", { "sketchPlane" : qUnion([Q0])});
            skCircle(sketch, "E67.0", {"center": v(3.35, 12.5) * mm, "radius": 1.65 * mm});
            skCircle(sketch, "E68", {"center": v(3.35, 12.5) * mm, "radius": 3 * mm});
            skSolve(sketch);
        }
        {
            var Q0;
            Q0=qSketchRegion(id+"F29",true);
            extrude(context, id + "F30", {"entities" : qUnion([Q0]), "operationType" : NewBodyOperationType.ADD, "depth" : .5 * mm});
        }
        {
            var Q0;
            Q0=makeQuery(id+"F30.opExtrude","CAP_EDGE",EDGE,{"disambiguationData":[OSD([sQuery(id+"F29.wireOp",EDGE,"E68")])],"isStart":false});
            var Q1;
            Q1=makeQuery(id+"F28.opExtrude","CAP_EDGE",EDGE,{"disambiguationData":[OSD([sQuery(id+"F27.wireOp",EDGE,"E65")])],"isStart":false});
            var Q2;
            Q2=makeQuery(id+"F26.opExtrude","CAP_EDGE",EDGE,{"disambiguationData":[OSD([sQuery(id+"F25.wireOp",EDGE,"E64")])],"isStart":false});
            var Q3;
            Q3=makeQuery(id+"F24.opExtrude","CAP_EDGE",EDGE,{"disambiguationData":[OSD([sQuery(id+"F23.wireOp",EDGE,"E62")])],"isStart":false});
            chamfer(context, id + "F31", {"entities" : qUnion([Q0, Q1, Q2, Q3]), "width" : .5 * mm, "tangentPropagation" : true});
        }
        {
            var Q0;
            Q0=makeQuery(id+"F9.boolean.opBoolean","MERGE",FACE,{"derivedFrom":[makeQuery(id+"F1.opExtrude","SWEPT_FACE",FACE,{"disambiguationData":[OSD([sQuery(id+"F0.wireOp",EDGE,"E0.top")])]}),makeQuery(id+"F9.opExtrude","SWEPT_FACE",FACE,{"disambiguationData":[OSD([sQuery(id+"F8.wireOp",EDGE,"E36.top")])]}),makeQuery(id+"F9.opExtrude","SWEPT_FACE",FACE,{"disambiguationData":[OSD([sQuery(id+"F8.wireOp",EDGE,"E37.bottom")])]})]});
            var sketch = newSketch(context, id + "F32", { "sketchPlane" : qUnion([Q0])});
            skLineSegment(sketch, "E69", {"start": v(-39, 0) * mm, "end": v(-36, 3) * mm});
            skLineSegment(sketch, "E70", {"start": v(-36, 3) * mm, "end": v(-28, 3) * mm});
            skLineSegment(sketch, "E71", {"start": v(-28, 3) * mm, "end": v(-25, 0) * mm});
            skLineSegment(sketch, "E72", {"start": v(-39, 0) * mm, "end": v(-25, 0) * mm});
            skSolve(sketch);
        }
        {
            var Q0;
            Q0=qSketchRegion(id+"F32",true);
            extrude(context, id + "F33", {"entities" : qUnion([Q0]), "operationType" : NewBodyOperationType.REMOVE, "endBound" : BoundingType.THROUGH_ALL, "oppositeDirection" : true, "depth" : 25 * mm});
        }
        {
            var Q0;
            Q0=makeQuery(id+"F5.opExtrude","SWEPT_FACE",FACE,{"disambiguationData":[OSD([sQuery(id+"F4.wireOp",EDGE,"E10.right")])]});
            var sketch = newSketch(context, id + "F34", { "sketchPlane" : qUnion([Q0])});
            skLineSegment(sketch, "E73.0", {"start": v(29.1, 19.35) * mm, "end": v(29.1, 19.35) * mm});
            skCircle(sketch, "E74", {"center": v(25, 17.5) * mm, "radius": 2.75 * mm});
            skSolve(sketch);
        }
        {
            var Q0;
            Q0=qSketchRegion(id+"F34",true);
            var Q1;
            Q1=makeQuery(id+"F3.opExtrude","SWEPT_FACE",FACE,{"disambiguationData":[OSD([sQuery(id+"F2.wireOp",EDGE,"E5.left")])]});
            extrude(context, id + "F35", {"entities" : qUnion([Q0]), "operationType" : NewBodyOperationType.REMOVE, "endBound" : BoundingType.UP_TO_SURFACE, "oppositeDirection" : true, "endBoundEntityFace" : qUnion([Q1]), "depth" : 25 * mm});
        }
        {
            var Q0;
            {var subQ0=sQuery(id+"F0.wireOp",EDGE,"E1");var subQ1=makeQuery(id+"F1.opExtrude","SWEPT_FACE",FACE,{"disambiguationData":[OSD([subQ0])]});var subQ2=sQuery(id+"F0.wireOp",EDGE,"E0.right");var subQ3=sQuery(id+"F0.wireOp",EDGE,"E0.top");var subQ7=sQuery(id+"F0.wireOp",EDGE,"E0.left");var subQ8=sQuery(id+"F0.wireOp",EDGE,"E4");var subQ9=sQuery(id+"F0.wireOp",EDGE,"E3");var subQ10=sQuery(id+"F0.wireOp",EDGE,"E0.bottom");Q0=makeQuery(id+"F9.boolean.opBoolean","SPLIT",FACE,{"disambiguationData":[TD([subQ1])],"derivedFrom":makeQuery(id+"F3.boolean.opBoolean","SPLIT",FACE,{"disambiguationData":[TD([makeQuery(id+"F1.opExtrude","SWEPT_FACE",FACE,{"disambiguationData":[OSD([subQ10])]})])],"derivedFrom":makeQuery(id+"F1.opExtrude","CAP_FACE",FACE,{"disambiguationData":[OSD([subQ10,subQ3,subQ7,subQ2,subQ0,subQ9,subQ8])],"isStart":false})})});}
            var sketch = newSketch(context, id + "F36", { "sketchPlane" : qUnion([Q0])});
            skCircle(sketch, "E75.0", {"center": v(58, 44) * mm, "radius": 2.65 * mm, "construction": true});
            skCircle(sketch, "E76.0", {"center": v(58, 6) * mm, "radius": 2.65 * mm, "construction": true});
            skCircle(sketch, "E77.cCircle", {"center": v(58, 44) * mm, "radius": 3.95 * mm, "construction": true});
            skLineSegment(sketch, "E77.0", {"start": v(61.8, 46.53) * mm, "end": v(62.09, 41.97) * mm});
            skLineSegment(sketch, "E77.1", {"start": v(62.09, 41.97) * mm, "end": v(58.29, 39.45) * mm});
            skLineSegment(sketch, "E77.2", {"start": v(58.29, 39.45) * mm, "end": v(54.2, 41.47) * mm});
            skLineSegment(sketch, "E77.3", {"start": v(54.2, 41.47) * mm, "end": v(53.91, 46.03) * mm});
            skLineSegment(sketch, "E77.4", {"start": v(53.91, 46.03) * mm, "end": v(57.71, 48.55) * mm});
            skLineSegment(sketch, "E77.5", {"start": v(57.71, 48.55) * mm, "end": v(61.8, 46.53) * mm});
            skPoint(sketch, "E77.0.midPoint", {"position": v(61.94, 44.25) * mm});
            skCircle(sketch, "E78.cCircle", {"center": v(58, 6) * mm, "radius": 4.09 * mm, "construction": true});
            skLineSegment(sketch, "E78.0", {"start": v(62.09, 8.36) * mm, "end": v(62.09, 3.64) * mm});
            skLineSegment(sketch, "E78.1", {"start": v(62.09, 3.64) * mm, "end": v(58, 1.28) * mm});
            skLineSegment(sketch, "E78.2", {"start": v(58, 1.28) * mm, "end": v(53.91, 3.64) * mm});
            skLineSegment(sketch, "E78.3", {"start": v(53.91, 3.64) * mm, "end": v(53.91, 8.36) * mm});
            skLineSegment(sketch, "E78.4", {"start": v(53.91, 8.36) * mm, "end": v(58, 10.72) * mm});
            skLineSegment(sketch, "E78.5", {"start": v(58, 10.72) * mm, "end": v(62.09, 8.36) * mm});
            skPoint(sketch, "E78.0.midPoint", {"position": v(62.09, 6) * mm});
            skSolve(sketch);
        }
        {
            var Q0;
            {var subQ1=sQuery(id+"F0.wireOp",EDGE,"E4");var subQ2=makeQuery(id+"F1.opExtrude","SWEPT_FACE",FACE,{"disambiguationData":[OSD([subQ1])]});var subQ5=sQuery(id+"F0.wireOp",EDGE,"E0.left");var subQ7=sQuery(id+"F0.wireOp",EDGE,"E3");var subQ8=sQuery(id+"F0.wireOp",EDGE,"E1");var subQ9=sQuery(id+"F0.wireOp",EDGE,"E0.bottom");var subQ10=sQuery(id+"F0.wireOp",EDGE,"E0.right");var subQ11=sQuery(id+"F0.wireOp",EDGE,"E0.top");Q0=makeQuery(id+"F9.boolean.opBoolean","SPLIT",FACE,{"disambiguationData":[TD([subQ2])],"derivedFrom":makeQuery(id+"F3.boolean.opBoolean","SPLIT",FACE,{"disambiguationData":[TD([makeQuery(id+"F1.opExtrude","SWEPT_FACE",FACE,{"disambiguationData":[OSD([subQ9])]})])],"derivedFrom":makeQuery(id+"F1.opExtrude","CAP_FACE",FACE,{"disambiguationData":[OSD([subQ9,subQ11,subQ5,subQ10,subQ8,subQ7,subQ1])],"isStart":false})})});}
            var sketch = newSketch(context, id + "F37", { "sketchPlane" : qUnion([Q0])});
            skCircle(sketch, "E79.0", {"center": v(6, 25) * mm, "radius": 2.65 * mm, "construction": true});
            skCircle(sketch, "E80.cCircle", {"center": v(6, 25) * mm, "radius": 3.95 * mm, "construction": true});
            skLineSegment(sketch, "E80.0", {"start": v(2.05, 22.72) * mm, "end": v(2.05, 27.28) * mm});
            skLineSegment(sketch, "E80.1", {"start": v(2.05, 27.28) * mm, "end": v(6, 29.56) * mm});
            skLineSegment(sketch, "E80.2", {"start": v(6, 29.56) * mm, "end": v(9.95, 27.28) * mm});
            skLineSegment(sketch, "E80.3", {"start": v(9.95, 27.28) * mm, "end": v(9.95, 22.72) * mm});
            skLineSegment(sketch, "E80.4", {"start": v(9.95, 22.72) * mm, "end": v(6, 20.44) * mm});
            skLineSegment(sketch, "E80.5", {"start": v(6, 20.44) * mm, "end": v(2.05, 22.72) * mm});
            skPoint(sketch, "E80.0.midPoint", {"position": v(2.05, 25) * mm});
            skSolve(sketch);
        }
        {
            var Q0;
            Q0=makeQuery(id+"F37.imprint","IMPRINT",FACE,{"disambiguationData":[TD([[makeQuery(id+"F37.imprint","IMPRINT",EDGE,{"derivedFrom":sQuery(id+"F37.wireOp",EDGE,"E80.0")}),1.0]])]});
            var Q1;
            {var subQ0=sQuery(id+"F37.wireOp",EDGE,"E80.3");var subQ1=makeQuery(id+"F3.opExtrude","CAP_EDGE",EDGE,{"disambiguationData":[OSD([sQuery(id+"F2.wireOp",EDGE,"E7")])],"isStart":true});var subQ2=makeQuery(id+"F37.imprint","INTERSECT",VERTEX,{"disambiguationData":[OD(0.0)],"derivedFrom":[subQ1,subQ0]});Q1=makeQuery(id+"F37.imprint","IMPRINT",FACE,{"disambiguationData":[TD([[makeQuery(id+"F37.imprint","IMPRINT",EDGE,{"disambiguationData":[TD([[subQ2,-1.0]])],"derivedFrom":subQ0}),1.0]])]});}
            var Q2;
            {var subQ0=sQuery(id+"F0.wireOp",EDGE,"E0.top");var subQ3=sQuery(id+"F0.wireOp",EDGE,"E0.left");var subQ5=sQuery(id+"F0.wireOp",EDGE,"E4");var subQ6=sQuery(id+"F0.wireOp",EDGE,"E3");var subQ7=sQuery(id+"F0.wireOp",EDGE,"E1");var subQ8=sQuery(id+"F0.wireOp",EDGE,"E0.bottom");var subQ9=sQuery(id+"F0.wireOp",EDGE,"E0.right");Q2=makeQuery(id+"F9.boolean.opBoolean","SPLIT",FACE,{"disambiguationData":[TD([makeQuery(id+"F9.opExtrude","SWEPT_FACE",FACE,{"disambiguationData":[OSD([sQuery(id+"F8.wireOp",EDGE,"E37.right")])]})])],"derivedFrom":makeQuery(id+"F3.boolean.opBoolean","SPLIT",FACE,{"disambiguationData":[TD([makeQuery(id+"F1.opExtrude","SWEPT_FACE",FACE,{"disambiguationData":[OSD([subQ8])]})])],"derivedFrom":makeQuery(id+"F1.opExtrude","CAP_FACE",FACE,{"disambiguationData":[OSD([subQ8,subQ0,subQ3,subQ9,subQ7,subQ6,subQ5])],"isStart":false})})});}
            var Q3;
            {var subQ1=sQuery(id+"F0.wireOp",EDGE,"E0.bottom");var subQ2=makeQuery(id+"F1.opExtrude","SWEPT_FACE",FACE,{"disambiguationData":[OSD([subQ1])]});var subQ3=sQuery(id+"F0.wireOp",EDGE,"E0.left");var subQ5=sQuery(id+"F0.wireOp",EDGE,"E4");var subQ6=sQuery(id+"F0.wireOp",EDGE,"E3");var subQ7=sQuery(id+"F0.wireOp",EDGE,"E1");var subQ8=sQuery(id+"F0.wireOp",EDGE,"E0.right");var subQ9=sQuery(id+"F0.wireOp",EDGE,"E0.top");Q3=makeQuery(id+"F9.boolean.opBoolean","SPLIT",FACE,{"disambiguationData":[TD([makeQuery(id+"F9.opExtrude","SWEPT_FACE",FACE,{"disambiguationData":[OSD([sQuery(id+"F8.wireOp",EDGE,"E39.right")])]})])],"derivedFrom":makeQuery(id+"F3.boolean.opBoolean","SPLIT",FACE,{"disambiguationData":[TD([subQ2])],"derivedFrom":makeQuery(id+"F1.opExtrude","CAP_FACE",FACE,{"disambiguationData":[OSD([subQ1,subQ9,subQ3,subQ8,subQ7,subQ6,subQ5])],"isStart":false})})});}
            var Q4;
            {var subQ0=makeQuery(id+"F3.opExtrude","SWEPT_FACE",FACE,{"disambiguationData":[OSD([sQuery(id+"F2.wireOp",EDGE,"E5.right")])]});var subQ1=sQuery(id+"F0.wireOp",EDGE,"E0.right");var subQ3=sQuery(id+"F0.wireOp",EDGE,"E0.left");var subQ4=sQuery(id+"F0.wireOp",EDGE,"E4");var subQ5=sQuery(id+"F0.wireOp",EDGE,"E3");var subQ6=sQuery(id+"F0.wireOp",EDGE,"E1");var subQ7=sQuery(id+"F0.wireOp",EDGE,"E0.bottom");var subQ8=sQuery(id+"F0.wireOp",EDGE,"E0.top");Q4=makeQuery(id+"F9.boolean.opBoolean","SPLIT",FACE,{"disambiguationData":[TD([subQ0])],"derivedFrom":makeQuery(id+"F3.boolean.opBoolean","SPLIT",FACE,{"disambiguationData":[TD([makeQuery(id+"F1.opExtrude","SWEPT_FACE",FACE,{"disambiguationData":[OSD([subQ7])]})])],"derivedFrom":makeQuery(id+"F1.opExtrude","CAP_FACE",FACE,{"disambiguationData":[OSD([subQ7,subQ8,subQ3,subQ1,subQ6,subQ5,subQ4])],"isStart":false})})});}
            var Q5;
            Q5=makeQuery(id+"F36.imprint","IMPRINT",FACE,{"disambiguationData":[TD([[makeQuery(id+"F36.imprint","IMPRINT",EDGE,{"derivedFrom":sQuery(id+"F36.wireOp",EDGE,"E77.0")}),1.0]])]});
            extrude(context, id + "F38", {"entities" : qUnion([Q0, Q1, Q2, Q3, Q4, Q5]), "operationType" : NewBodyOperationType.ADD, "depth" : 2.5 * mm});
        }
        {
            var Q0;
            {var subQ0=sQuery(id+"F0.wireOp",EDGE,"E0.right");var subQ1=sQuery(id+"F0.wireOp",EDGE,"E0.bottom");var subQ2=makeQuery(id+"F1.opExtrude","SWEPT_FACE",FACE,{"disambiguationData":[OSD([subQ1])]});var subQ4=sQuery(id+"F0.wireOp",EDGE,"E3");var subQ5=makeQuery(id+"F1.opExtrude","SWEPT_FACE",FACE,{"disambiguationData":[OSD([subQ4])]});var subQ7=sQuery(id+"F0.wireOp",EDGE,"E0.left");var subQ8=sQuery(id+"F0.wireOp",EDGE,"E4");var subQ9=sQuery(id+"F0.wireOp",EDGE,"E1");var subQ10=sQuery(id+"F0.wireOp",EDGE,"E0.top");Q0=makeQuery(id+"F9.boolean.opBoolean","SPLIT",FACE,{"disambiguationData":[TD([subQ5])],"derivedFrom":makeQuery(id+"F3.boolean.opBoolean","SPLIT",FACE,{"disambiguationData":[TD([subQ2])],"derivedFrom":makeQuery(id+"F1.opExtrude","CAP_FACE",FACE,{"disambiguationData":[OSD([subQ1,subQ10,subQ7,subQ0,subQ9,subQ4,subQ8])],"isStart":false})})});}
            var sketch = newSketch(context, id + "F39", { "sketchPlane" : qUnion([Q0])});
            skCircle(sketch, "E81.cCircle", {"center": v(58, 6) * mm, "radius": 3.95 * mm, "construction": true});
            skLineSegment(sketch, "E81.0", {"start": v(61.95, 8.28) * mm, "end": v(61.95, 3.72) * mm});
            skLineSegment(sketch, "E81.1", {"start": v(61.95, 3.72) * mm, "end": v(58, 1.44) * mm});
            skLineSegment(sketch, "E81.2", {"start": v(58, 1.44) * mm, "end": v(54.05, 3.72) * mm});
            skLineSegment(sketch, "E81.3", {"start": v(54.05, 3.72) * mm, "end": v(54.05, 8.28) * mm});
            skLineSegment(sketch, "E81.4", {"start": v(54.05, 8.28) * mm, "end": v(58, 10.56) * mm});
            skLineSegment(sketch, "E81.5", {"start": v(58, 10.56) * mm, "end": v(61.95, 8.28) * mm});
            skPoint(sketch, "E81.0.midPoint", {"position": v(61.95, 6) * mm});
            skSolve(sketch);
        }
        {
            var Q0;
            Q0=makeQuery(id+"F39.imprint","IMPRINT",FACE,{"disambiguationData":[TD([[makeQuery(id+"F39.imprint","IMPRINT",EDGE,{"derivedFrom":sQuery(id+"F39.wireOp",EDGE,"E81.0")}),1.0]])]});
            extrude(context, id + "F40", {"entities" : qUnion([Q0]), "operationType" : NewBodyOperationType.ADD, "depth" : 2.5 * mm});
        }
        {
            var Q0;
            {var subQ0=makeQuery(id+"F3.opExtrude","SWEPT_FACE",FACE,{"disambiguationData":[OSD([sQuery(id+"F2.wireOp",EDGE,"E5.right")])]});var subQ1=sQuery(id+"F0.wireOp",EDGE,"E0.right");var subQ3=sQuery(id+"F0.wireOp",EDGE,"E0.left");var subQ4=sQuery(id+"F0.wireOp",EDGE,"E4");var subQ5=sQuery(id+"F0.wireOp",EDGE,"E3");var subQ6=sQuery(id+"F0.wireOp",EDGE,"E1");var subQ7=sQuery(id+"F0.wireOp",EDGE,"E0.bottom");var subQ8=sQuery(id+"F0.wireOp",EDGE,"E0.top");Q0=makeQuery(id+"F38.opExtrude","CAP_FACE",FACE,{"disambiguationData":[OSD([subQ7,subQ8,subQ3,subQ1,subQ6,subQ5,subQ4]),TDD([makeQuery(id+"F9.boolean.opBoolean","SPLIT",FACE,{"disambiguationData":[TD([subQ0])],"derivedFrom":makeQuery(id+"F3.boolean.opBoolean","SPLIT",FACE,{"disambiguationData":[TD([makeQuery(id+"F1.opExtrude","SWEPT_FACE",FACE,{"disambiguationData":[OSD([subQ7])]})])],"derivedFrom":makeQuery(id+"F1.opExtrude","CAP_FACE",FACE,{"disambiguationData":[OSD([subQ7,subQ8,subQ3,subQ1,subQ6,subQ5,subQ4])],"isStart":false})})})])],"isStart":false});}
            var sketch = newSketch(context, id + "F41", { "sketchPlane" : qUnion([Q0])});
            skLineSegment(sketch, "E82.0.0", {"start": v(0, 35.15) * mm, "end": v(1.12, 35.15) * mm});
            skLineSegment(sketch, "E82.0.1", {"start": v(1.12, 35.15) * mm, "end": v(7.85, 35.15) * mm});
            skLineSegment(sketch, "E82.0.2", {"start": v(7.85, 35.15) * mm, "end": v(7.85, 39.15) * mm});
            skLineSegment(sketch, "E82.0.3", {"start": v(7.85, 39.15) * mm, "end": v(1.12, 39.15) * mm});
            skLineSegment(sketch, "E82.0.4", {"start": v(1.12, 39.15) * mm, "end": v(0, 39.15) * mm});
            skLineSegment(sketch, "E82.0.5", {"start": v(0, 39.15) * mm, "end": v(0, 35.15) * mm});
            skLineSegment(sketch, "E83.0.0", {"start": v(56.15, 35.15) * mm, "end": v(62.88, 35.15) * mm});
            skLineSegment(sketch, "E83.0.1", {"start": v(62.88, 35.15) * mm, "end": v(64, 35.15) * mm});
            skLineSegment(sketch, "E83.0.2", {"start": v(64, 35.15) * mm, "end": v(64, 39.15) * mm});
            skLineSegment(sketch, "E83.0.3", {"start": v(64, 39.15) * mm, "end": v(62.88, 39.15) * mm});
            skLineSegment(sketch, "E83.0.4", {"start": v(62.88, 39.15) * mm, "end": v(56.15, 39.15) * mm});
            skLineSegment(sketch, "E83.0.5", {"start": v(56.15, 39.15) * mm, "end": v(56.15, 35.15) * mm});
            skLineSegment(sketch, "E84.0.0", {"start": v(56.15, 14.85) * mm, "end": v(56.15, 10.85) * mm});
            skLineSegment(sketch, "E84.0.1", {"start": v(56.15, 10.85) * mm, "end": v(62.88, 10.85) * mm});
            skLineSegment(sketch, "E84.0.2", {"start": v(62.88, 10.85) * mm, "end": v(64, 10.85) * mm});
            skLineSegment(sketch, "E84.0.3", {"start": v(64, 10.85) * mm, "end": v(64, 14.85) * mm});
            skLineSegment(sketch, "E84.0.4", {"start": v(64, 14.85) * mm, "end": v(62.88, 14.85) * mm});
            skLineSegment(sketch, "E84.0.5", {"start": v(62.88, 14.85) * mm, "end": v(56.15, 14.85) * mm});
            skLineSegment(sketch, "E85.0.0", {"start": v(0, 14.85) * mm, "end": v(0, 10.85) * mm});
            skLineSegment(sketch, "E85.0.1", {"start": v(0, 10.85) * mm, "end": v(1.12, 10.85) * mm});
            skLineSegment(sketch, "E85.0.2", {"start": v(1.12, 10.85) * mm, "end": v(7.85, 10.85) * mm});
            skLineSegment(sketch, "E85.0.3", {"start": v(7.85, 10.85) * mm, "end": v(7.85, 14.85) * mm});
            skLineSegment(sketch, "E85.0.4", {"start": v(7.85, 14.85) * mm, "end": v(1.12, 14.85) * mm});
            skLineSegment(sketch, "E85.0.5", {"start": v(1.12, 14.85) * mm, "end": v(0, 14.85) * mm});
            skSolve(sketch);
        }
        {
            var Q0;
            Q0=qSketchRegion(id+"F41",true);
            extrude(context, id + "F42", {"entities" : qUnion([Q0]), "operationType" : NewBodyOperationType.ADD, "endBound" : BoundingType.UP_TO_NEXT, "oppositeDirection" : true, "depth" : 25 * mm});
        }
        {
            var Q0;
            {var subQ1=sQuery(id+"F0.wireOp",EDGE,"E0.left");var subQ7=makeQuery(id+"F1.opExtrude","CAP_EDGE",EDGE,{"disambiguationData":[OSD([subQ1])],"isStart":false});Q0=makeQuery(id+"F42.boolean.opBoolean","MERGE",EDGE,{"derivedFrom":[makeQuery(id+"F38.opExtrude","CAP_EDGE",EDGE,{"disambiguationData":[OSD([subQ1]),TDD([makeQuery(id+"F9.boolean.opBoolean","SPLIT",EDGE,{"disambiguationData":[TD([makeQuery(id+"F3.opExtrude","SWEPT_FACE",FACE,{"disambiguationData":[OSD([sQuery(id+"F2.wireOp",EDGE,"E5.top")])]})])],"derivedFrom":subQ7})])],"isStart":false}),makeQuery(id+"F38.opExtrude","CAP_EDGE",EDGE,{"disambiguationData":[OSD([subQ1]),TDD([makeQuery(id+"F9.boolean.opBoolean","SPLIT",EDGE,{"disambiguationData":[TD([makeQuery(id+"F3.opExtrude","SWEPT_FACE",FACE,{"disambiguationData":[OSD([sQuery(id+"F2.wireOp",EDGE,"E5.bottom")])]})])],"derivedFrom":subQ7})])],"isStart":false}),makeQuery(id+"F38.opExtrude","CAP_EDGE",EDGE,{"disambiguationData":[OSD([subQ1]),TDD([makeQuery(id+"F37.imprint","IMPRINT",EDGE,{"derivedFrom":makeQuery(id+"F9.boolean.opBoolean","SPLIT",EDGE,{"disambiguationData":[TD([makeQuery(id+"F9.opExtrude","SWEPT_FACE",FACE,{"disambiguationData":[OSD([sQuery(id+"F8.wireOp",EDGE,"E27.top")])]})])],"derivedFrom":subQ7})})])],"isStart":false}),makeQuery(id+"F42.opExtrude","CAP_EDGE",EDGE,{"disambiguationData":[OSD([sQuery(id+"F41.wireOp",EDGE,"E82.0.5")])],"isStart":true}),makeQuery(id+"F42.opExtrude","CAP_EDGE",EDGE,{"disambiguationData":[OSD([sQuery(id+"F41.wireOp",EDGE,"E85.0.0")])],"isStart":true})]});}
            var Q1;
            {var subQ0=sQuery(id+"F0.wireOp",EDGE,"E0.left");var subQ1=sQuery(id+"F0.wireOp",EDGE,"E4");var subQ2=sQuery(id+"F0.wireOp",EDGE,"E3");var subQ3=sQuery(id+"F0.wireOp",EDGE,"E1");var subQ4=sQuery(id+"F0.wireOp",EDGE,"E0.bottom");var subQ5=sQuery(id+"F0.wireOp",EDGE,"E0.right");var subQ6=sQuery(id+"F0.wireOp",EDGE,"E0.top");Q1=makeQuery(id+"F38.opExtrude","CAP_EDGE",EDGE,{"disambiguationData":[OSD([subQ4,subQ6,subQ0,subQ5,subQ3,subQ2,subQ1]),TDD([makeQuery(id+"F36.imprint","IMPRINT",EDGE,{"derivedFrom":makeQuery(id+"F7.opFillet","BLEND_EDGE",EDGE,{"blendedFrom":[makeQuery(id+"F1.opExtrude","SWEPT_EDGE",EDGE,{"disambiguationData":[OSD([subQ6,subQ5])]}),makeQuery(id+"F3.boolean.opBoolean","SPLIT",FACE,{"disambiguationData":[TD([makeQuery(id+"F1.opExtrude","SWEPT_FACE",FACE,{"disambiguationData":[OSD([subQ4])]})])],"derivedFrom":makeQuery(id+"F1.opExtrude","CAP_FACE",FACE,{"disambiguationData":[OSD([subQ4,subQ6,subQ0,subQ5,subQ3,subQ2,subQ1])],"isStart":false})})],"blendedInto":[makeQuery(id+"F3.boolean.opBoolean","SPLIT",FACE,{"disambiguationData":[TD([makeQuery(id+"F1.opExtrude","SWEPT_FACE",FACE,{"disambiguationData":[OSD([subQ4])]})])],"derivedFrom":makeQuery(id+"F1.opExtrude","CAP_FACE",FACE,{"disambiguationData":[OSD([subQ4,subQ6,subQ0,subQ5,subQ3,subQ2,subQ1])],"isStart":false})})]})})])],"isStart":false});}
            chamfer(context, id + "F43", {"entities" : qUnion([Q0, Q1]), "width" : 1 * mm, "tangentPropagation" : true});
        }
        {
            var Q0;
            {var subQ2=sQuery(id+"F2.wireOp",EDGE,"E5.top");Q0=makeQuery(id+"F42.boolean.opBoolean","INTERSECT",EDGE,{"derivedFrom":[makeQuery(id+"F11.boolean.opBoolean","COPY",FACE,{"disambiguationData":[TD([makeQuery(id+"F3.opExtrude","SWEPT_FACE",FACE,{"disambiguationData":[OSD([subQ2])]})])],"derivedFrom":makeQuery(id+"F11.opExtrude","SWEPT_FACE",FACE,{"disambiguationData":[OSD([sQuery(id+"F10.wireOp",EDGE,"E47")])]})}),makeQuery(id+"F42.opExtrude","CAP_FACE",FACE,{"disambiguationData":[OSD([sQuery(id+"F41.wireOp",EDGE,"E85.0.0"),sQuery(id+"F41.wireOp",EDGE,"E85.0.1"),sQuery(id+"F41.wireOp",EDGE,"E85.0.2"),sQuery(id+"F41.wireOp",EDGE,"E85.0.3"),sQuery(id+"F41.wireOp",EDGE,"E85.0.4"),sQuery(id+"F41.wireOp",EDGE,"E85.0.5")])],"isStart":true})]});}
            var Q1;
            {var subQ4=sQuery(id+"F2.wireOp",EDGE,"E5.bottom");Q1=makeQuery(id+"F42.boolean.opBoolean","INTERSECT",EDGE,{"derivedFrom":[makeQuery(id+"F11.boolean.opBoolean","COPY",FACE,{"disambiguationData":[TD([makeQuery(id+"F3.opExtrude","SWEPT_FACE",FACE,{"disambiguationData":[OSD([subQ4])]})])],"derivedFrom":makeQuery(id+"F11.opExtrude","SWEPT_FACE",FACE,{"disambiguationData":[OSD([sQuery(id+"F10.wireOp",EDGE,"E47")])]})}),makeQuery(id+"F42.opExtrude","CAP_FACE",FACE,{"disambiguationData":[OSD([sQuery(id+"F41.wireOp",EDGE,"E82.0.0"),sQuery(id+"F41.wireOp",EDGE,"E82.0.1"),sQuery(id+"F41.wireOp",EDGE,"E82.0.2"),sQuery(id+"F41.wireOp",EDGE,"E82.0.3"),sQuery(id+"F41.wireOp",EDGE,"E82.0.4"),sQuery(id+"F41.wireOp",EDGE,"E82.0.5")])],"isStart":true})]});}
            var Q2;
            {var subQ4=sQuery(id+"F2.wireOp",EDGE,"E5.bottom");Q2=makeQuery(id+"F42.boolean.opBoolean","INTERSECT",EDGE,{"derivedFrom":[makeQuery(id+"F11.boolean.opBoolean","COPY",FACE,{"disambiguationData":[TD([makeQuery(id+"F3.opExtrude","SWEPT_FACE",FACE,{"disambiguationData":[OSD([subQ4])]})])],"derivedFrom":makeQuery(id+"F11.opExtrude","SWEPT_FACE",FACE,{"disambiguationData":[OSD([sQuery(id+"F10.wireOp",EDGE,"E44")])]})}),makeQuery(id+"F42.opExtrude","CAP_FACE",FACE,{"disambiguationData":[OSD([sQuery(id+"F41.wireOp",EDGE,"E83.0.0"),sQuery(id+"F41.wireOp",EDGE,"E83.0.1"),sQuery(id+"F41.wireOp",EDGE,"E83.0.2"),sQuery(id+"F41.wireOp",EDGE,"E83.0.3"),sQuery(id+"F41.wireOp",EDGE,"E83.0.4"),sQuery(id+"F41.wireOp",EDGE,"E83.0.5")])],"isStart":true})]});}
            var Q3;
            {var subQ0=sQuery(id+"F2.wireOp",EDGE,"E5.top");Q3=makeQuery(id+"F42.boolean.opBoolean","INTERSECT",EDGE,{"derivedFrom":[makeQuery(id+"F11.boolean.opBoolean","COPY",FACE,{"disambiguationData":[TD([makeQuery(id+"F3.opExtrude","SWEPT_FACE",FACE,{"disambiguationData":[OSD([subQ0])]})])],"derivedFrom":makeQuery(id+"F11.opExtrude","SWEPT_FACE",FACE,{"disambiguationData":[OSD([sQuery(id+"F10.wireOp",EDGE,"E44")])]})}),makeQuery(id+"F42.opExtrude","CAP_FACE",FACE,{"disambiguationData":[OSD([sQuery(id+"F41.wireOp",EDGE,"E84.0.0"),sQuery(id+"F41.wireOp",EDGE,"E84.0.1"),sQuery(id+"F41.wireOp",EDGE,"E84.0.2"),sQuery(id+"F41.wireOp",EDGE,"E84.0.3"),sQuery(id+"F41.wireOp",EDGE,"E84.0.4"),sQuery(id+"F41.wireOp",EDGE,"E84.0.5")])],"isStart":true})]});}
            fillet(context, id + "F44", {"entities" : qUnion([Q0, Q1, Q2, Q3]), "radius" : 5 * mm, "tangentPropagation" : true, "allowEdgeOverflow" : false});
        }
        {
            var Q0;
            Q0=makeQuery(id+"F3.opExtrude","SWEPT_FACE",FACE,{"disambiguationData":[OSD([sQuery(id+"F2.wireOp",EDGE,"E5.left")])]});
            var sketch = newSketch(context, id + "F45", { "sketchPlane" : qUnion([Q0])});
            skLineSegment(sketch, "E86.0.0", {"start": v(-49, 7.5) * mm, "end": v(-50, 6.5) * mm, "construction": true});
            skLineSegment(sketch, "E86.0.1", {"start": v(-44, 6.5) * mm, "end": v(-50, 6.5) * mm, "construction": true});
            skLineSegment(sketch, "E86.0.2", {"start": v(-44, 6.5) * mm, "end": v(-44, 7.5) * mm, "construction": true});
            skLineSegment(sketch, "E86.0.3", {"start": v(-44, 7.5) * mm, "end": v(-49, 7.5) * mm, "construction": true});
            skLineSegment(sketch, "E87.0.0", {"start": v(-44, 7.5) * mm, "end": v(-44, 6.5) * mm, "construction": true});
            skLineSegment(sketch, "E87.0.1", {"start": v(-44, 6.5) * mm, "end": v(-6, 6.5) * mm, "construction": true});
            skLineSegment(sketch, "E87.0.2", {"start": v(-6, 6.5) * mm, "end": v(-6, 7.5) * mm, "construction": true});
            skLineSegment(sketch, "E87.0.3", {"start": v(-6, 7.5) * mm, "end": v(-39.15, 7.5) * mm, "construction": true});
            skLineSegment(sketch, "E87.0.4", {"start": v(-14.85, 7.5) * mm, "end": v(-39.15, 7.5) * mm, "construction": true});
            skLineSegment(sketch, "E87.0.5", {"start": v(-14.85, 7.5) * mm, "end": v(-39.15, 7.5) * mm, "construction": true});
            skLineSegment(sketch, "E87.0.6", {"start": v(-39.15, 7.5) * mm, "end": v(-39.15, 7.5) * mm});
            skLineSegment(sketch, "E87.0.7", {"start": v(-39.15, 7.5) * mm, "end": v(-44, 7.5) * mm, "construction": true});
            skLineSegment(sketch, "E88.0.0", {"start": v(-50, 16.5) * mm, "end": v(-50, 6.5) * mm, "construction": true});
            skLineSegment(sketch, "E88.0.1", {"start": v(-50, 6.5) * mm, "end": v(-49, 7.5) * mm, "construction": true});
            skLineSegment(sketch, "E88.0.2", {"start": v(-49, 7.5) * mm, "end": v(-39.15, 7.5) * mm, "construction": true});
            skLineSegment(sketch, "E88.0.3", {"start": v(-39.15, 7.5) * mm, "end": v(-39.15, 22.5) * mm, "construction": true});
            skLineSegment(sketch, "E88.0.4", {"start": v(-39.15, 22.5) * mm, "end": v(-44, 22.5) * mm, "construction": true});
            skLineSegment(sketch, "E88.0.5", {"start": v(-44, 22.5) * mm, "end": v(-50, 16.5) * mm, "construction": true});
            skLineSegment(sketch, "E89.0.0", {"start": v(-39.15, 22.5) * mm, "end": v(-39.15, 8.4) * mm, "construction": true});
            skLineSegment(sketch, "E89.0.1", {"start": v(-39.15, 8.4) * mm, "end": v(-35.15, 8.4) * mm, "construction": true});
            skLineSegment(sketch, "E89.0.2", {"start": v(-35.15, 8.4) * mm, "end": v(-35.15, 22.5) * mm, "construction": true});
            skLineSegment(sketch, "E89.0.3", {"start": v(-35.15, 22.5) * mm, "end": v(-39.15, 22.5) * mm, "construction": true});
            skLineSegment(sketch, "E90", {"start": v(-49, 7.5) * mm, "end": v(-39.15, 7.5) * mm});
            skLineSegment(sketch, "E91", {"start": v(-39.15, 15.25) * mm, "end": v(-39.15, 7.5) * mm});
            skLineSegment(sketch, "E92", {"start": v(-49, 7.5) * mm, "end": v(-49, 15.25) * mm});
            skLineSegment(sketch, "E93", {"start": v(-49, 15.25) * mm, "end": v(-39.15, 15.25) * mm});
            skCircle(sketch, "E94", {"center": v(-44, 10.25) * mm, "radius": 2.75 * mm});
            skSolve(sketch);
        }
        {
            var Q0;
            Q0 = qSketchRegion(id + "F45", true);
            extrude(context, id + "F46", {"entities" : qUnion([Q0]), "operationType" : NewBodyOperationType.ADD, "oppositeDirection" : true, "depth" : 7.5 * mm});
        }
        {
            var Q0;
            Q0=makeQuery(id+"F46.opExtrude","CAP_FACE",FACE,{"disambiguationData":[OSD([sQuery(id+"F45.wireOp",EDGE,"E90"),sQuery(id+"F45.wireOp",EDGE,"E91"),sQuery(id+"F45.wireOp",EDGE,"E92"),sQuery(id+"F45.wireOp",EDGE,"E93")])],"isStart":true});
            var sketch = newSketch(context, id + "F47", { "sketchPlane" : qUnion([Q0])});
            skCircle(sketch, "E95", {"center": v(-44, 9.45) * mm, "radius": 1.95 * mm});
            skLineSegment(sketch, "E96.0.0", {"start": v(-49, 7.5) * mm, "end": v(-39.15, 7.5) * mm, "construction": true});
            skLineSegment(sketch, "E96.0.1", {"start": v(-39.15, 7.5) * mm, "end": v(-39.15, 15.25) * mm, "construction": true});
            skLineSegment(sketch, "E96.0.2", {"start": v(-39.15, 15.25) * mm, "end": v(-49, 15.25) * mm, "construction": true});
            skLineSegment(sketch, "E96.0.3", {"start": v(-49, 15.25) * mm, "end": v(-49, 7.5) * mm, "construction": true});
            skSolve(sketch);
        }
        {
            var Q0;
            Q0=makeQuery(id+"F47.imprint","IMPRINT",FACE,{"disambiguationData":[TD([[makeQuery(id+"F47.imprint","IMPRINT",EDGE,{"derivedFrom":sQuery(id+"F47.wireOp",EDGE,"E95")}),1.0]])]});
            var Q1;
            Q1=makeQuery(id+"F46.opExtrude","CAP_FACE",FACE,{"disambiguationData":[OSD([sQuery(id+"F45.wireOp",EDGE,"E90"),sQuery(id+"F45.wireOp",EDGE,"E91"),sQuery(id+"F45.wireOp",EDGE,"E92"),sQuery(id+"F45.wireOp",EDGE,"E93")])],"isStart":false});
            extrude(context, id + "F48", {"entities" : qUnion([Q0]), "operationType" : NewBodyOperationType.REMOVE, "endBound" : BoundingType.UP_TO_SURFACE, "oppositeDirection" : true, "endBoundEntityFace" : qUnion([Q1]), "depth" : 25 * mm});
        }
        {
            var Q0;
            Q0=makeQuery(id+"F46.opExtrude","SWEPT_EDGE",EDGE,{"disambiguationData":[OSD([sQuery(id+"F45.wireOp",EDGE,"E92"),sQuery(id+"F45.wireOp",EDGE,"E93")])]});
            chamfer(context, id + "F49", {"entities" : qUnion([Q0]), "width" : 5 * mm, "tangentPropagation" : true});
        }
        {
            var Q0;
            Q0=makeQuery(id+"F46.opExtrude","CAP_EDGE",EDGE,{"disambiguationData":[OSD([sQuery(id+"F45.wireOp",EDGE,"E93")])],"isStart":true});
            var Q1;
            {var subQ0=sQuery(id+"F45.wireOp",EDGE,"E93");var subQ1=sQuery(id+"F45.wireOp",EDGE,"E92");Q1=makeQuery(id+"F49.opChamfer","BLEND_EDGE",EDGE,{"blendedFrom":[makeQuery(id+"F46.opExtrude","SWEPT_EDGE",EDGE,{"disambiguationData":[OSD([subQ1,subQ0])]}),makeQuery(id+"F46.opExtrude","CAP_FACE",FACE,{"disambiguationData":[OSD([sQuery(id+"F45.wireOp",EDGE,"E90"),sQuery(id+"F45.wireOp",EDGE,"E91"),subQ1,subQ0])],"isStart":true})],"blendedInto":[makeQuery(id+"F46.opExtrude","CAP_FACE",FACE,{"disambiguationData":[OSD([sQuery(id+"F45.wireOp",EDGE,"E90"),sQuery(id+"F45.wireOp",EDGE,"E91"),subQ1,subQ0])],"isStart":true})]});}
            var Q2;
            Q2=makeQuery(id+"F46.opExtrude","CAP_EDGE",EDGE,{"disambiguationData":[OSD([sQuery(id+"F45.wireOp",EDGE,"E92")])],"isStart":true});
            chamfer(context, id + "F50", {"entities" : qUnion([Q0, Q1, Q2]), "width" : 1.5 * mm, "tangentPropagation" : true});
        }
        {
            var Q0;
            Q0=makeQuery(id+"F9.boolean.opBoolean","MERGE",EDGE,{"disambiguationData":[OD(2.0)],"derivedFrom":[makeQuery(id+"F3.opExtrude","CAP_EDGE",EDGE,{"disambiguationData":[OSD([sQuery(id+"F2.wireOp",EDGE,"E5.top")])],"isStart":true}),makeQuery(id+"F9.opExtrude","CAP_EDGE",EDGE,{"disambiguationData":[OSD([sQuery(id+"F8.wireOp",EDGE,"E28.bottom")])],"isStart":true}),makeQuery(id+"F9.opExtrude","CAP_EDGE",EDGE,{"disambiguationData":[OSD([sQuery(id+"F8.wireOp",EDGE,"E30.bottom")])],"isStart":true})]});
            var Q1;
            Q1=makeQuery(id+"F9.boolean.opBoolean","MERGE",EDGE,{"disambiguationData":[OD(2.0)],"derivedFrom":[makeQuery(id+"F3.opExtrude","CAP_EDGE",EDGE,{"disambiguationData":[OSD([sQuery(id+"F2.wireOp",EDGE,"E5.bottom")])],"isStart":true}),makeQuery(id+"F9.opExtrude","CAP_EDGE",EDGE,{"disambiguationData":[OSD([sQuery(id+"F8.wireOp",EDGE,"E27.bottom")])],"isStart":true}),makeQuery(id+"F9.opExtrude","CAP_EDGE",EDGE,{"disambiguationData":[OSD([sQuery(id+"F8.wireOp",EDGE,"E29.bottom")])],"isStart":true})]});
            fillet(context, id + "F51", {"entities" : qUnion([Q0, Q1]), "radius" : 5 * mm, "tangentPropagation" : true, "allowEdgeOverflow" : false});
        }
    });
